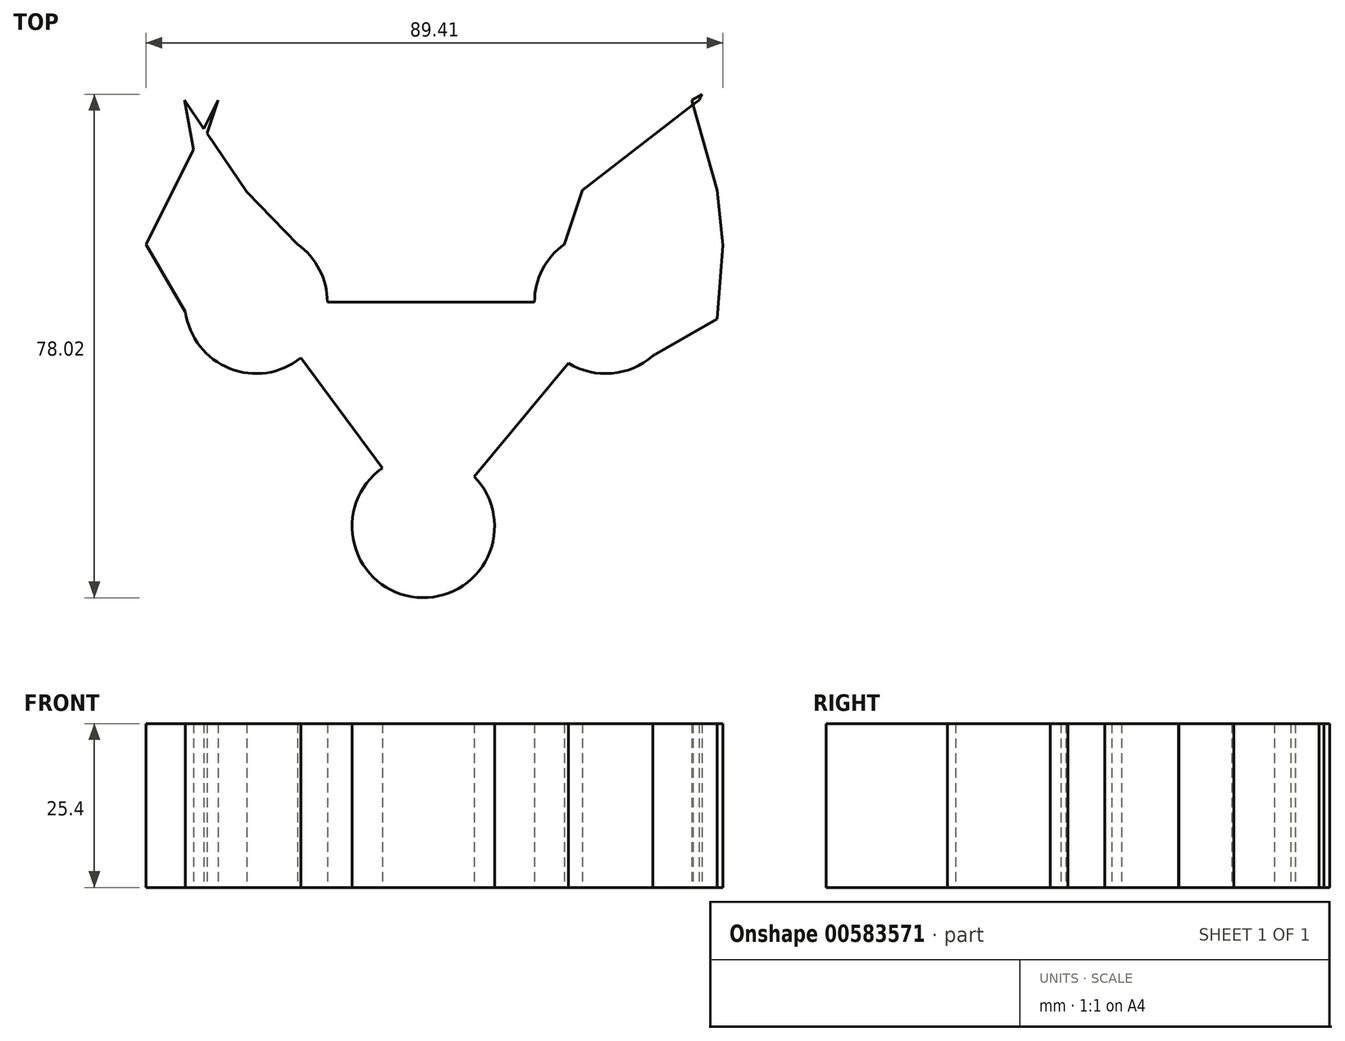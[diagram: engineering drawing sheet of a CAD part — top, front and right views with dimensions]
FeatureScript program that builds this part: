
annotation { "Feature Type Name" : "Feature", "Feature Type Description" : "" }
export const myFeature = defineFeature(function(context is Context, id is Id, definition is map)
    precondition{}
    {
        {
            var Q0;
            Q0=qCreatedBy(makeId("Top.planeOp"),FACE);
            var sketch = newSketch(context, id + "F0", { "sketchPlane" : qUnion([Q0])});
            skCircle(sketch, "E0", {"center": v(-44.78, 42.25) * mm, "radius": 11.05 * mm});
            skCircle(sketch, "E1", {"center": v(9.41, 42.25) * mm, "radius": 11.05 * mm});
            skCircle(sketch, "E2", {"center": v(-18.87, 7.52) * mm, "radius": 11.05 * mm});
            skLineSegment(sketch, "E3", {"start": v(-37.87, 33.63) * mm, "end": v(-24.26, 15.26) * mm});
            skLineSegment(sketch, "E4", {"start": v(-10.98, 15.26) * mm, "end": v(3.63, 32.84) * mm});
            skLineSegment(sketch, "E5", {"start": v(-33.73, 42.28) * mm, "end": v(-1.64, 42.28) * mm});
            skLineSegment(sketch, "E6", {"start": v(5.81, 59.64) * mm, "end": v(2.98, 51.24) * mm});
            skLineSegment(sketch, "E7", {"start": v(5.81, 59.64) * mm, "end": v(23.86, 73.6) * mm});
            skLineSegment(sketch, "E8", {"start": v(23.86, 73.6) * mm, "end": v(24.3, 74.5) * mm});
            skLineSegment(sketch, "E9", {"start": v(22.74, 73.6) * mm, "end": v(24.3, 74.5) * mm});
            skLineSegment(sketch, "E10", {"start": v(22.74, 73.6) * mm, "end": v(26.7, 59.64) * mm});
            skLineSegment(sketch, "E11", {"start": v(26.7, 59.64) * mm, "end": v(27.56, 51.1) * mm});
            skLineSegment(sketch, "E12", {"start": v(27.56, 51.14) * mm, "end": v(27.56, 51.1) * mm});
            skLineSegment(sketch, "E13", {"start": v(27.56, 51.14) * mm, "end": v(26.7, 39.66) * mm});
            skLineSegment(sketch, "E14", {"start": v(26.7, 39.66) * mm, "end": v(16.7, 33.95) * mm});
            skLineSegment(sketch, "E15", {"start": v(23.86, 73.6) * mm, "end": v(22.74, 73.6) * mm});
            skLineSegment(sketch, "E16", {"start": v(-54.07, 63.53) * mm, "end": v(-55.9, 73.6) * mm});
            skLineSegment(sketch, "E17", {"start": v(-55.9, 73.6) * mm, "end": v(-46.21, 59.36) * mm});
            skLineSegment(sketch, "E18", {"start": v(-46.21, 59.36) * mm, "end": v(-38.34, 51.24) * mm});
            skLineSegment(sketch, "E19", {"start": v(-54.07, 63.53) * mm, "end": v(-50.67, 73.6) * mm});
            skLineSegment(sketch, "E20", {"start": v(-50.67, 73.6) * mm, "end": v(-60.45, 54.04) * mm});
            skLineSegment(sketch, "E21", {"start": v(-60.45, 54.04) * mm, "end": v(-61.85, 51.24) * mm});
            skLineSegment(sketch, "E22", {"start": v(-65.3, 42.33) * mm, "end": v(-60.45, 45.11) * mm});
            skPoint(sketch, "E23.end.orphan", {"position": v(-54.07, 37.9) * mm});
            skLineSegment(sketch, "E24", {"start": v(-61.85, 51.24) * mm, "end": v(-54.07, 37.9) * mm});
            skSolve(sketch);
        }
        {
            var Q0;
            Q0 = qSketchRegion(id + "F0", true);
            extrude(context, id + "F1", {"entities" : qUnion([Q0]), "depth" : 25.4 * mm, "offsetDistance" : 25.4 * mm});
        }
    });
